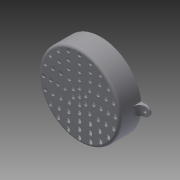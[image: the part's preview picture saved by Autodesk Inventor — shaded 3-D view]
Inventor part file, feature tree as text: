
AUTODESK INVENTOR PART (.ipt)
format: ipt  version: 2014 (Build 180170000, 170)  size: 352,256 bytes
history: native  units: mm
features: extrude x4, sketch x4, fillet x3, other x1
ambient origin geometry x8: Origin, YZ Plane, XZ Plane, XY Plane, X Axis, Y Axis, Z Axis, Center Point
bodies: Body1 (feature_tree)
feature tree (12):
  other  "ソリッド1"
  extrude  "押し出し1"  Depth=60.0mm
  extrude  "押し出し2"  Depth=16.0mm TaperAngle=0.0deg
  extrude  "押し出し3"  Depth=58.0mm
  extrude  "押し出し4"  Depth=15.0mm TaperAngle=0.0deg
  fillet  "フィレット1"  Radius=3.0mm
  fillet  "フィレット2"  Radius=3.0mm
  fillet  "フィレット3"  Radius=3.0mm
  sketch  "スケッチ1"
  sketch  "スケッチ2"
  sketch  "スケッチ3"
  sketch  "スケッチ4"
